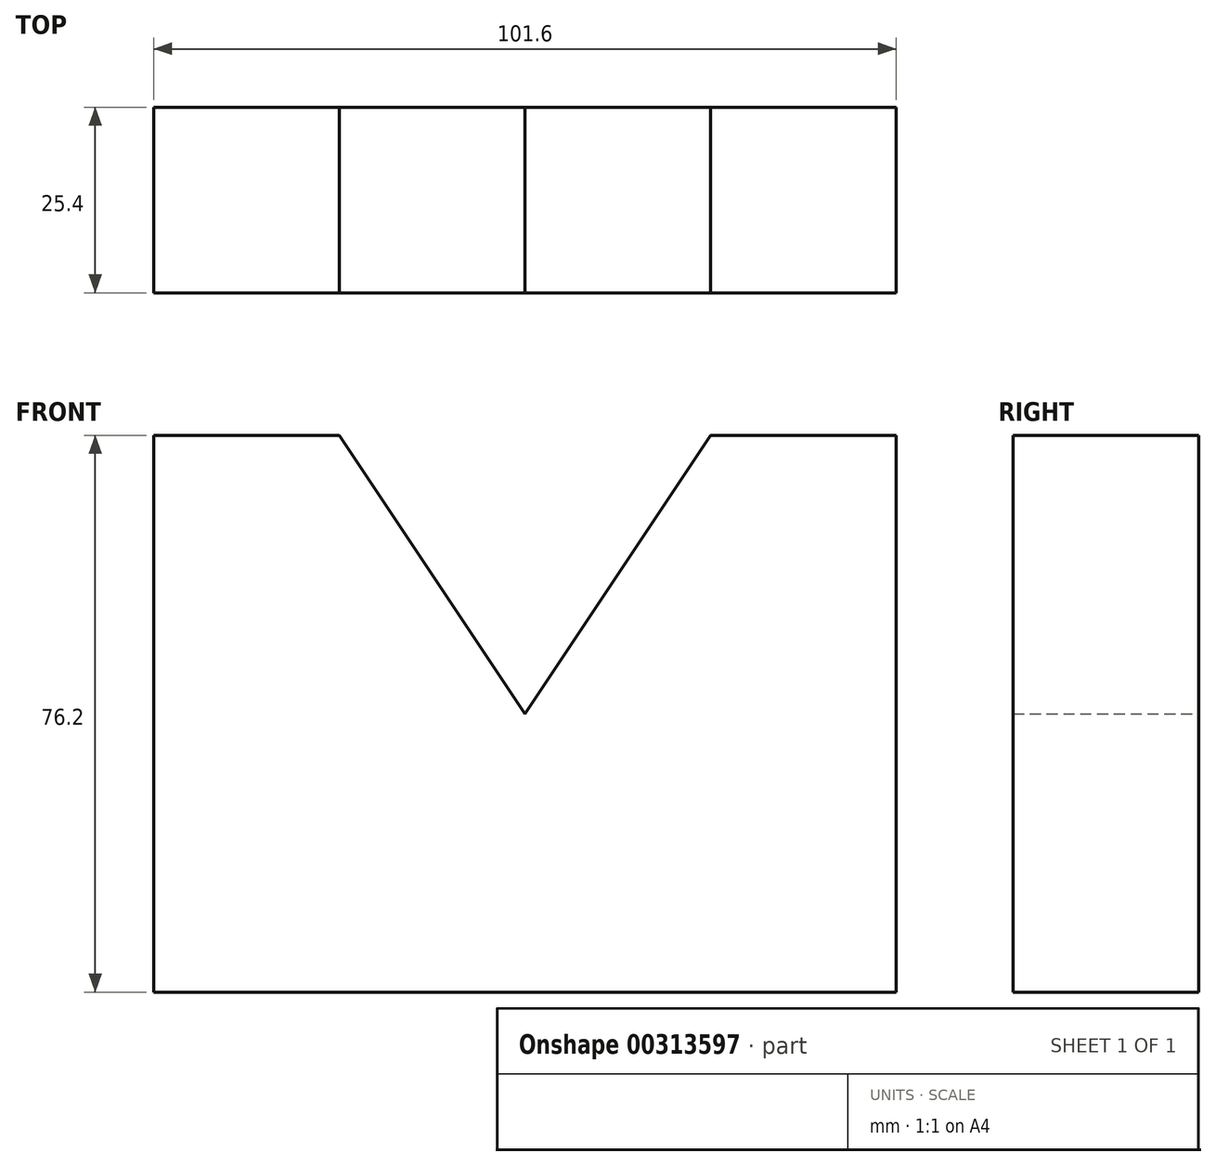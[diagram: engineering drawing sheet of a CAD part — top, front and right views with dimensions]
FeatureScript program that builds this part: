
annotation { "Feature Type Name" : "Feature", "Feature Type Description" : "" }
export const myFeature = defineFeature(function(context is Context, id is Id, definition is map)
    precondition{}
    {
        {
            var Q0;
            Q0=qCreatedBy(makeId("Front.planeOp"),FACE);
            var sketch = newSketch(context, id + "F0", { "sketchPlane" : qUnion([Q0])});
            skLineSegment(sketch, "E0", {"start": v(-21.29, 31.52) * mm, "end": v(-46.69, 31.52) * mm});
            skLineSegment(sketch, "E1", {"start": v(-46.69, 31.52) * mm, "end": v(-46.69, -44.68) * mm});
            skLineSegment(sketch, "E2", {"start": v(-46.69, -44.68) * mm, "end": v(54.91, -44.68) * mm});
            skLineSegment(sketch, "E3", {"start": v(54.91, -44.68) * mm, "end": v(54.91, 31.52) * mm});
            skLineSegment(sketch, "E4", {"start": v(54.91, 31.52) * mm, "end": v(29.51, 31.52) * mm});
            skLineSegment(sketch, "E5", {"start": v(29.51, 31.52) * mm, "end": v(4.11, -6.58) * mm});
            skLineSegment(sketch, "E6", {"start": v(-21.29, 31.52) * mm, "end": v(4.11, -6.58) * mm});
            skSolve(sketch);
        }
        {
            var Q0;
            Q0=makeQuery(id+"F0.imprint","IMPRINT",FACE,{"disambiguationData":[TD([[makeQuery(id+"F0.imprint","IMPRINT",EDGE,{"derivedFrom":sQuery(id+"F0.wireOp",EDGE,"E0")}),1.0]])]});
            extrude(context, id + "F1", {"entities" : qUnion([Q0]), "depth" : 25.4 * mm});
        }
    });
